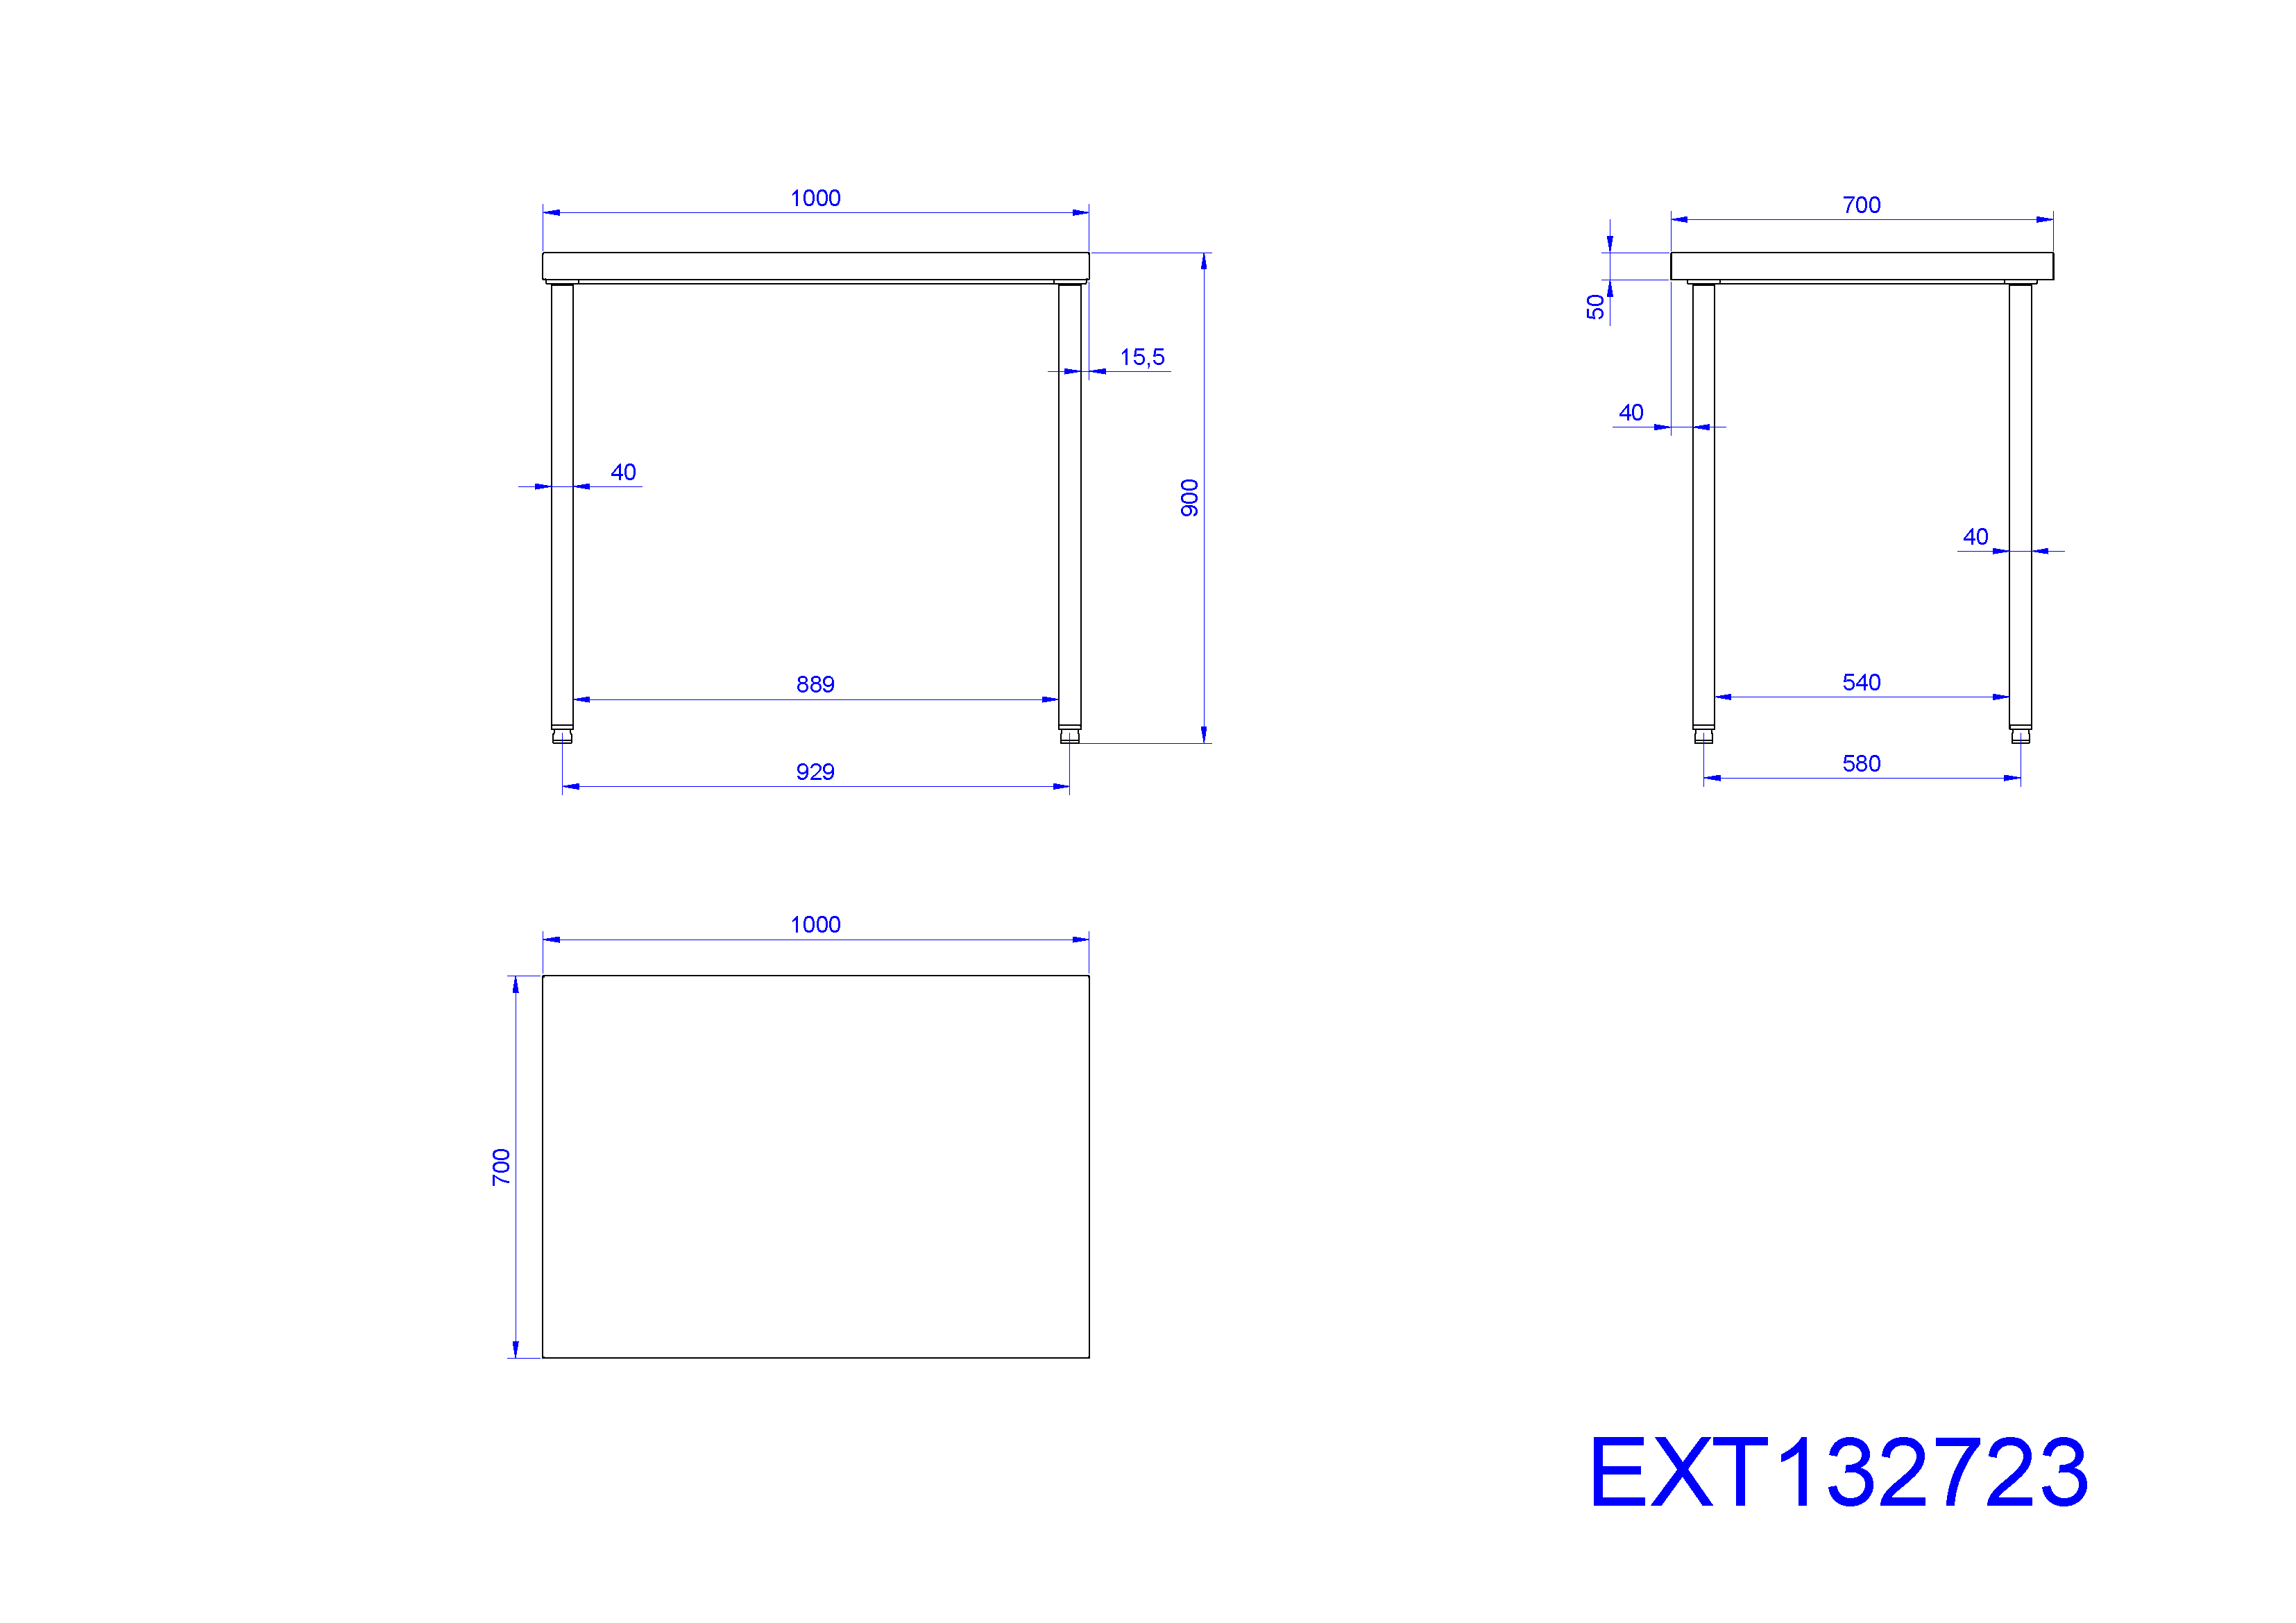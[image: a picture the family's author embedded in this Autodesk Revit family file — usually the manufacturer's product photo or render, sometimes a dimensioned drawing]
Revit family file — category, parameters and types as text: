
# Revit family: QF_ELECTROLUXPROFESSIONAL_132729_TG2400PN
name_source: partatom
category: Attrezzature speciali
units: mm (PartAtom-declared; Revit-internal decimal feet)

## family parameters
Basato su piano di lavoro = No
Condiviso = No
Punto di calcolo locali = No
Quota connettore circolare = Usa diametro
Sempre verticale = Sì
Taglio con vuoti quando caricato = No
Tipo di parte = Normale

## types (1)
- Standard
    Accessory = Sì
    Cold Water Size = 0 mm
    Compressed Air Pressure = 0.0 Pa
    Compressed Air Size = 0 mm
    Compressed Air Volume = 0.0 L/s
    Condensate Return Size = 0 mm
    Cycle = 0 Hz
    Depth Actual = 700 mm  [stored 2.29659 ft]
    Descrizione = WORK TABLE 2400 MM
    Direct Waste Size = 0 mm
    Gas Input Pressure = 0
    Gas KW = 0
    Gas Size = 0 mm
    HP = 0 HP
    Height Actual = 900 mm  [stored 2.95276 ft]
    Hot Water Size = 0 mm
    Item Number = 132729
    Length Actual = 2400 mm  [stored 7.87402 ft]
    Modello = TG2400PN
    Phase = 0
    Produttore = Electrolux Professional
    Prospetto di default = 0 mm  [stored 0 ft]
    Refrigerant Compressor Remote = Sì
    Refrigeration Liquid Line Size = 0 mm  [stored 0 ft]
    Refrigeration Suction Line Size = 0 mm  [stored 0 ft]
    Steam Consumption per Hour = 0
    Steam Supply Maximum Pressure = 0.0 Pa
    Steam Supply Minimum Pressure = 0.0 Pa
    Steam Supply Size = 0 mm
    URL = https://www.electroluxprofessional.com
    URL Manufacturer = https://www.electroluxprofessional.com
    Volts = 0 V
    Watts = 0 W
    Weight = 84.00 kg

note: source unit labels omitted for Gas Input Pressure — the stored unit's dimension contradicts the parameter name (converter mislabeling)

note: [stored X ft] marks values corroborated as IEEE doubles in the binary element streams (Revit-internal decimal feet)

## geometry (parser evidence)
native form markers: Sweep x2
no freeform markers — native parametric forms only
